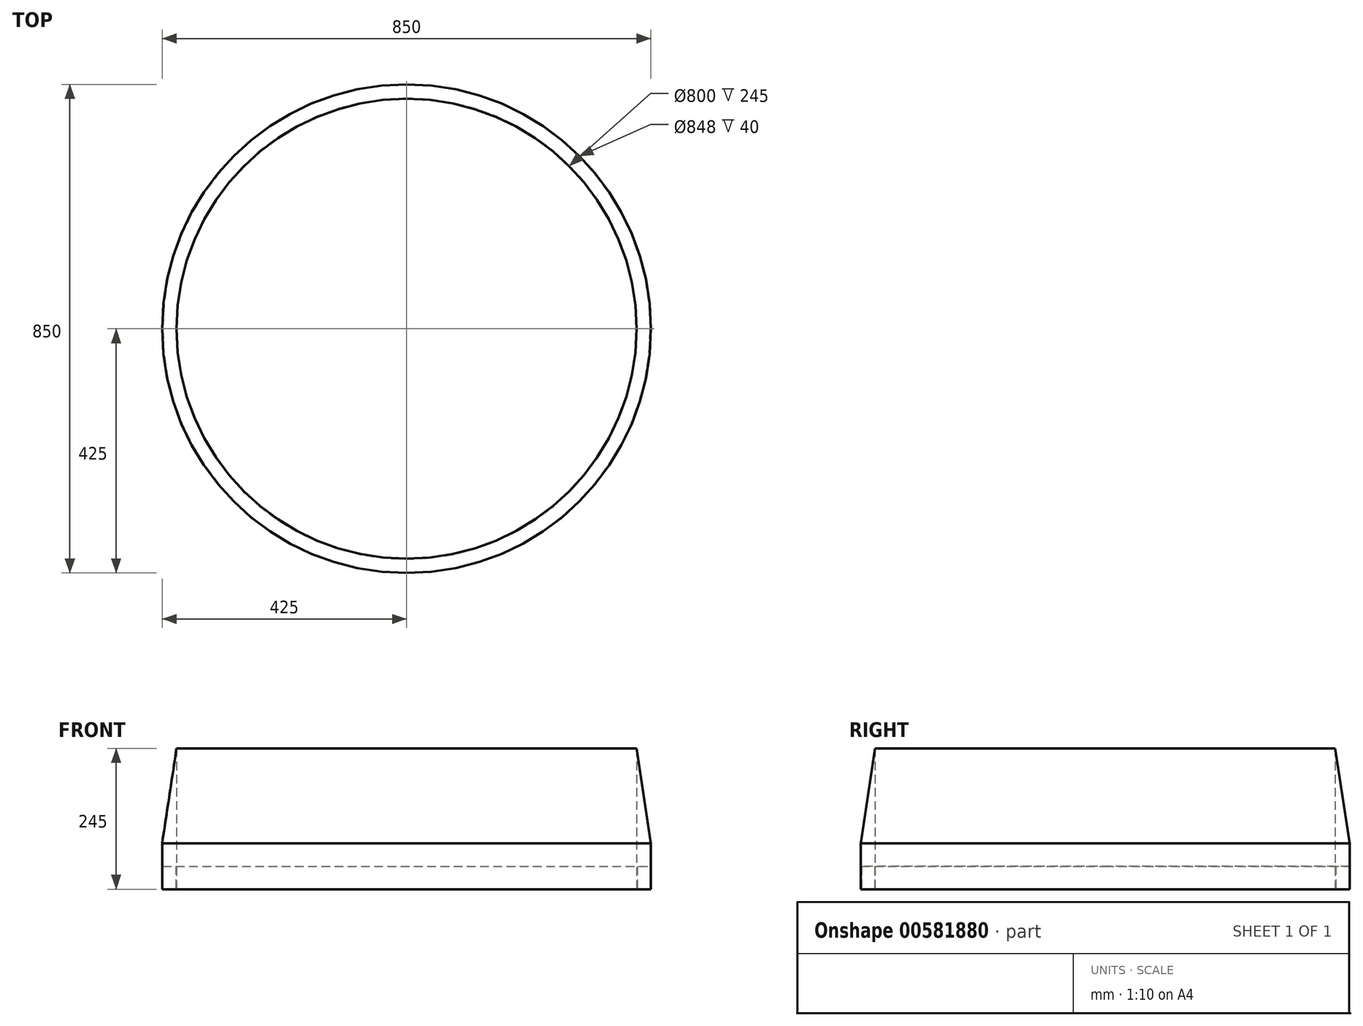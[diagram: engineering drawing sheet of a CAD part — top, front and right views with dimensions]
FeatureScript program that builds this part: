
annotation { "Feature Type Name" : "Feature", "Feature Type Description" : "" }
export const myFeature = defineFeature(function(context is Context, id is Id, definition is map)
    precondition{}
    {
        {
            var Q0;
            Q0=qCreatedBy(makeId("Front.planeOp"),FACE);
            var sketch = newSketch(context, id + "F0", { "sketchPlane" : qUnion([Q0])});
            skLineSegment(sketch, "E0", {"start": v(0, -139.25) * mm, "end": v(0, 240.83) * mm, "construction": true});
            skLineSegment(sketch, "E1", {"start": v(-400, -67.22) * mm, "end": v(-400, 177.78) * mm});
            skLineSegment(sketch, "E2", {"start": v(-400, 177.78) * mm, "end": v(-425, 12.78) * mm});
            skLineSegment(sketch, "E3", {"start": v(-425, 12.78) * mm, "end": v(-425, -67.22) * mm});
            skLineSegment(sketch, "E4", {"start": v(-425, -67.22) * mm, "end": v(-424, -67.22) * mm});
            skLineSegment(sketch, "E5", {"start": v(-424, -67.22) * mm, "end": v(-424, -27.22) * mm});
            skLineSegment(sketch, "E6", {"start": v(-424, -27.22) * mm, "end": v(-401, -27.22) * mm});
            skLineSegment(sketch, "E7", {"start": v(-401, -27.22) * mm, "end": v(-401, -67.22) * mm});
            skLineSegment(sketch, "E8", {"start": v(-401, -67.22) * mm, "end": v(-400, -67.22) * mm});
            skSolve(sketch);
        }
        {
            var Q0;
            Q0=qSketchRegion(id+"F0",true);
            var Q1;
            Q1=sQuery(id+"F0.wireOp",EDGE,"E0");
            revolve(context, id + "F1", {"entities" : qUnion([Q0]), "axis" : qUnion([Q1]), "revolveType" : RevolveType.FULL});
        }
    });
